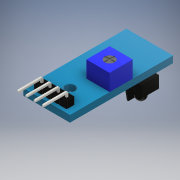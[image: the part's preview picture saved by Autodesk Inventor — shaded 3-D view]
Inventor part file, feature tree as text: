
AUTODESK INVENTOR PART (.ipt)
format: ipt  version: 2017 SP1 (Build 210196100, 196)  size: 402,432 bytes
history: native  units: mm
features: sketch x13, extrude x9, chamfer x7, fillet x3, pattern_linear x2, plane x2, revolve x2, projected_geometry x2, other x1, hole x1, sweep x1
ambient origin geometry x8: Origin, YZ Plane, XZ Plane, XY Plane, X Axis, Y Axis, Z Axis, Center Point
bodies: Body1 (feature_tree)
feature tree (43):
  other  "Sólido1"
  extrude  "Extrusión1"  Depth=31.0mm
  hole  "Agujero1"  [1 undecoded]
  extrude  "Extrusión3"  Depth=0.01mm
  extrude  "Extrusión4"  Depth=3.0mm
  extrude  "Extrusión5"  Depth=3.5mm
  extrude  "Extrusión6"  Depth=0.5mm
  fillet  "Empalme1"  Radius=0.5mm
  pattern_linear  "Patrón rectangular4"  Spacing1=2.0mm  [1 undecoded]
  sketch  "Boceto8"  dims[d32=3.5mm d33=3.5mm]
  plane  "Plano de trabajo1"
  sweep  "Barrido1"
  chamfer  "Chaflán1"  Distance=0.54mm
  chamfer  "Chaflán2"  Distance=0.54mm
  chamfer  "Chaflán3"  Distance=1.25mm
  chamfer  "Chaflán4"  Distance=1.25mm
  pattern_linear  "Patrón rectangular5"  Spacing1=-1.25mm  [1 undecoded]
  fillet  "Empalme2"  Radius=0.2mm
  plane  "Plano de trabajo2"
  extrude  "Extrusión7"  TaperAngle=0.0deg  [1 undecoded]
  extrude  "Extrusión8"  Depth=0.05mm
  chamfer  "Chaflán5"  Distance=0.05mm
  chamfer  "Chaflán6"  Distance=0.05mm
  chamfer  "Chaflán7"  Distance=0.05mm
  fillet  "Empalme4"  Radius=2.5mm
  extrude  "Extrusión9"  Depth=0.05mm
  revolve  "Revolución1"  [1 undecoded]
  revolve  "Revolución2"  [1 undecoded]
  extrude  "Extrusión10"  Depth=5.5mm
  sketch  "Boceto1"  dims[d0=14.0mm d1=31.0mm]
  sketch  "Boceto3"  dims[d2=2.0mm d3=0.0mm]
  sketch  "Boceto5"  dims[d4=7.0mm d5=7.0mm d6=3.0mm d7=6.0mm d8=4.0mm d9=2.0mm d10=90.0deg d11=8.0mm d12=20.594885mm d17=7.0mm]
  sketch  "Boceto6"  dims[d18=7.0mm d19=0.01mm]
  projected_geometry  "Contorno proyectado1"
  sketch  "Boceto7"  dims[d20=5.0mm d21=0.0mm d31=3.0mm]
  sketch  "Boceto10"  dims[d34=0.01mm d35=0.0mm d36=0.5mm d37=0.5mm]
  sketch  "Boceto12"  dims[d38=0.2mm d39=0.0mm]
  projected_geometry  "Contorno proyectado2"
  sketch  "Boceto13"  dims[d40=2.5mm]
  sketch  "Boceto14"  dims[d41=2.5mm]
  sketch  "Boceto15"  dims[d42=1.0mm]
  sketch  "Boceto16"  dims[d43=2.0mm d44=0.0mm]
  sketch  "Boceto18"  dims[d45=0.3mm d49=2.0mm d56=40.0mm d58=2.51mm d59=0.54mm d60=0.54mm d61=1.25mm d62=1.25mm d70=-1.25mm d71=0.2mm d72=1.0mm d73=7.0mm d74=0.0mm d75=0.0mm d76=0.05mm d77=0.5mm d78=12.217305mm d79=0.05mm d80=0.5mm d81=12.217305mm d82=0.05mm d83=0.5mm d84=12.217305mm d85=0.05mm d86=0.5mm d87=12.217305mm d88=40.0mm d90=2.5mm d91=0.05mm d92=3.0mm d93=10.0mm d94=5.5mm d95=4.0mm d96=0.0mm d98=0.5mm d99=4.5mm d100=0.5mm d101=3.0mm d102=0.0mm d103=0.5mm d104=3.0mm d105=12.217305mm d106=0.5mm d107=3.0mm d108=12.217305mm d109=0.5mm d110=1.0mm d111=12.217305mm d112=0.1mm d113=3.0mm d114=3.0mm d115=2.25mm d116=2.25mm d117=2.25mm d118=2.25mm d119=1.0mm d120=0.0mm d121=90.0deg d122=90.0deg d123=1.0mm d124=1.0mm d125=1.0mm d126=1.0mm d127=1.5mm d128=1.5mm d129=1.0mm d130=1.0mm d131=1.0mm d132=1.0mm d133=1.5mm d134=1.5mm d135=1.0mm d136=1.0mm d137=0.0mm]
note: 6 required parameter values undecoded (feature->parameter linkage not recoverable at this tier; creation-order binding heuristic only, values carry confidence <= 0.55)